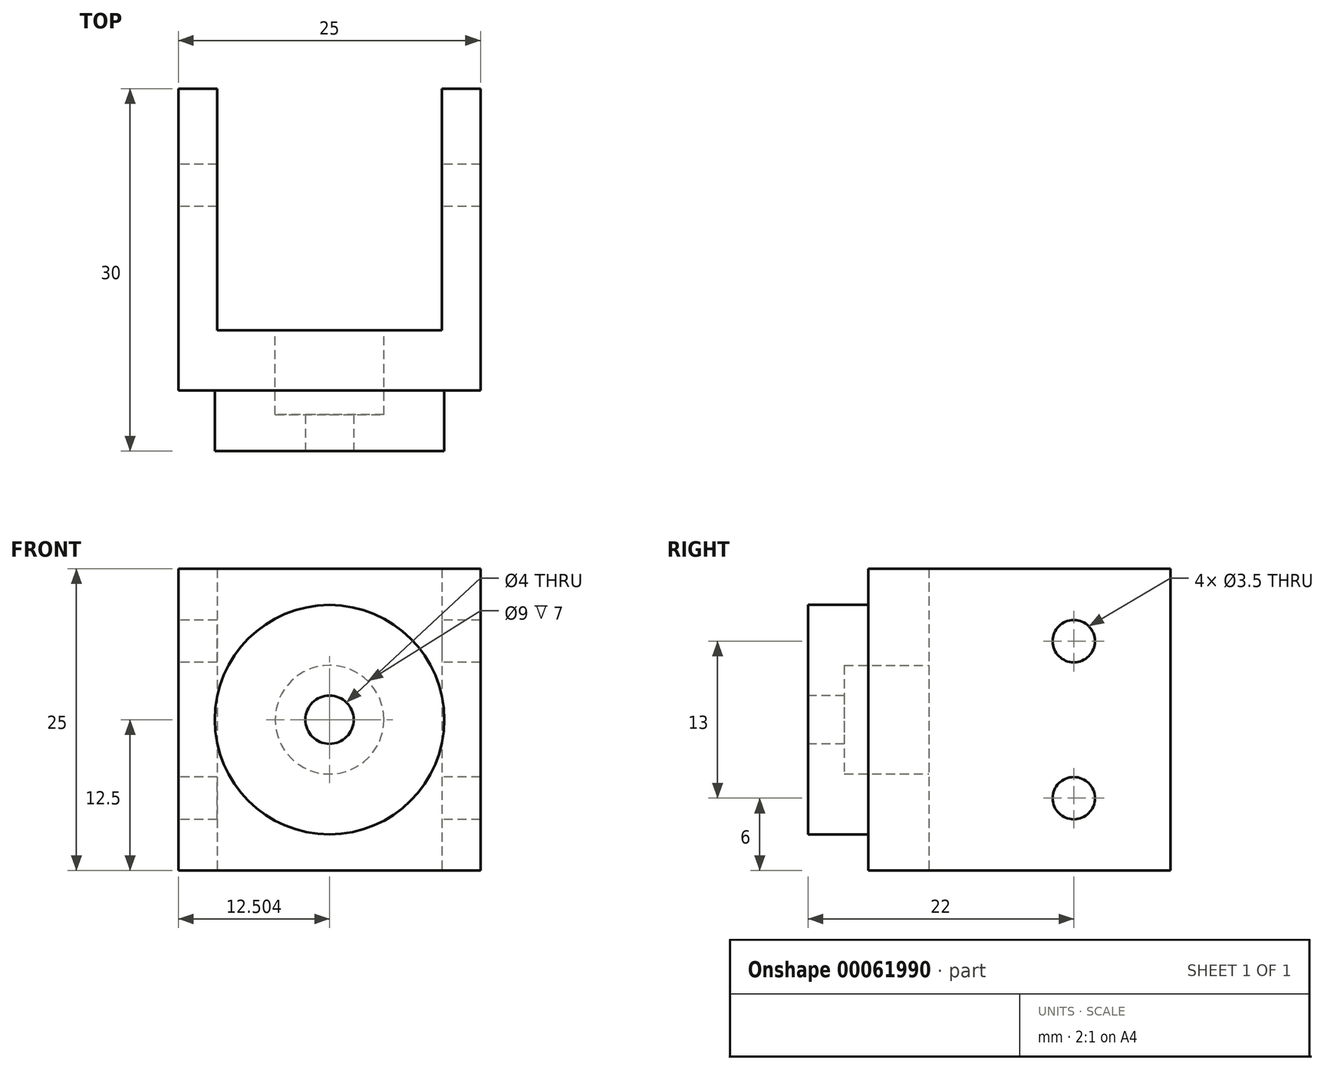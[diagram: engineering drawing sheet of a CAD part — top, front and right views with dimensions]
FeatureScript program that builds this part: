
annotation { "Feature Type Name" : "Feature", "Feature Type Description" : "" }
export const myFeature = defineFeature(function(context is Context, id is Id, definition is map)
    precondition{}
    {
        {
            var Q0;
            Q0=qCreatedBy(makeId("Top.planeOp"),FACE);
            var sketch = newSketch(context, id + "F0", { "sketchPlane" : qUnion([Q0])});
            skLineSegment(sketch, "E0.bottom", {"start": v(-12.37, 0) * mm, "end": v(12.63, 0) * mm});
            skLineSegment(sketch, "E0.top", {"start": v(-12.37, 25) * mm, "end": v(-9.17, 25) * mm});
            skLineSegment(sketch, "E0.left", {"start": v(-12.37, 0) * mm, "end": v(-12.37, 25) * mm});
            skLineSegment(sketch, "E0.right", {"start": v(12.63, 0) * mm, "end": v(12.63, 25) * mm});
            skLineSegment(sketch, "E1", {"start": v(-9.17, 25) * mm, "end": v(-9.17, 5) * mm});
            skLineSegment(sketch, "E2", {"start": v(-9.17, 5) * mm, "end": v(9.43, 5) * mm});
            skLineSegment(sketch, "E3", {"start": v(9.43, 5) * mm, "end": v(9.43, 25) * mm});
            skLineSegment(sketch, "E4.trimOffspring", {"start": v(9.43, 25) * mm, "end": v(12.63, 25) * mm});
            skSolve(sketch);
        }
        {
            var Q0;
            Q0=makeQuery(id+"F0.imprint","IMPRINT",FACE,{"disambiguationData":[TD([[makeQuery(id+"F0.imprint","IMPRINT",EDGE,{"derivedFrom":sQuery(id+"F0.wireOp",EDGE,"E0.bottom")}),1.0]])]});
            extrude(context, id + "F1", {"entities" : qUnion([Q0]), "depth" : 25 * mm});
        }
        {
            var Q0;
            Q0=makeQuery(id+"F1.opExtrude","SWEPT_FACE",FACE,{"disambiguationData":[OSD([sQuery(id+"F0.wireOp",EDGE,"E0.bottom")])]});
            var sketch = newSketch(context, id + "F2", { "sketchPlane" : qUnion([Q0])});
            skCircle(sketch, "E5", {"center": v(0.13, 12.5) * mm, "radius": 9.5 * mm});
            skPoint(sketch, "E5.centerSnap0", {"position": v(0.13, 25) * mm});
            skPoint(sketch, "E5.centerSnap1", {"position": v(12.63, 12.5) * mm});
            skSolve(sketch);
        }
        {
            var Q0;
            Q0=makeQuery(id+"F2.imprint","IMPRINT",FACE,{"disambiguationData":[TD([[makeQuery(id+"F2.imprint","IMPRINT",EDGE,{"derivedFrom":sQuery(id+"F2.wireOp",EDGE,"E5")}),1.0]])]});
            extrude(context, id + "F3", {"entities" : qUnion([Q0]), "operationType" : NewBodyOperationType.ADD, "depth" : 5 * mm});
        }
        {
            var Q0;
            Q0=makeQuery(id+"F3.opExtrude","CAP_FACE",FACE,{"disambiguationData":[OSD([sQuery(id+"F2.wireOp",EDGE,"E5")])],"isStart":false});
            var sketch = newSketch(context, id + "F4", { "sketchPlane" : qUnion([Q0])});
            skCircle(sketch, "E6", {"center": v(0.13, 12.5) * mm, "radius": 2 * mm});
            skSolve(sketch);
        }
        {
            var Q0;
            Q0=makeQuery(id+"F4.imprint","IMPRINT",FACE,{"disambiguationData":[TD([[makeQuery(id+"F4.imprint","IMPRINT",EDGE,{"derivedFrom":sQuery(id+"F4.wireOp",EDGE,"E6")}),1.0]])]});
            extrude(context, id + "F5", {"entities" : qUnion([Q0]), "operationType" : NewBodyOperationType.REMOVE, "endBound" : BoundingType.THROUGH_ALL, "oppositeDirection" : true, "depth" : 25 * mm});
        }
        {
            var Q0;
            Q0=makeQuery(id+"F1.opExtrude","SWEPT_FACE",FACE,{"disambiguationData":[OSD([sQuery(id+"F0.wireOp",EDGE,"E2")])]});
            var sketch = newSketch(context, id + "F6", { "sketchPlane" : qUnion([Q0])});
            skCircle(sketch, "E7", {"center": v(-0.13, 12.5) * mm, "radius": 4.5 * mm});
            skSolve(sketch);
        }
        {
            var Q0;
            Q0=makeQuery(id+"F6.imprint","IMPRINT",FACE,{"disambiguationData":[TD([[makeQuery(id+"F6.imprint","IMPRINT",EDGE,{"derivedFrom":sQuery(id+"F6.wireOp",EDGE,"E7")}),1.0]])]});
            extrude(context, id + "F7", {"entities" : qUnion([Q0]), "operationType" : NewBodyOperationType.REMOVE, "oppositeDirection" : true, "depth" : 7 * mm});
        }
        {
            var Q0;
            Q0=makeQuery(id+"F1.opExtrude","SWEPT_FACE",FACE,{"disambiguationData":[OSD([sQuery(id+"F0.wireOp",EDGE,"E0.left")])]});
            var sketch = newSketch(context, id + "F8", { "sketchPlane" : qUnion([Q0])});
            skCircle(sketch, "E8", {"center": v(-17, 6) * mm, "radius": 1.75 * mm});
            skCircle(sketch, "E9", {"center": v(-17, 19) * mm, "radius": 1.75 * mm});
            skSolve(sketch);
        }
        {
            var Q0;
            Q0=makeQuery(id+"F8.imprint","IMPRINT",FACE,{"disambiguationData":[TD([[makeQuery(id+"F8.imprint","IMPRINT",EDGE,{"derivedFrom":sQuery(id+"F8.wireOp",EDGE,"E8")}),1.0]])]});
            var Q1;
            Q1=makeQuery(id+"F8.imprint","IMPRINT",FACE,{"disambiguationData":[TD([[makeQuery(id+"F8.imprint","IMPRINT",EDGE,{"derivedFrom":sQuery(id+"F8.wireOp",EDGE,"E9")}),1.0]])]});
            extrude(context, id + "F9", {"entities" : qUnion([Q0, Q1]), "operationType" : NewBodyOperationType.REMOVE, "endBound" : BoundingType.THROUGH_ALL, "oppositeDirection" : true, "depth" : 25 * mm});
        }
    });
